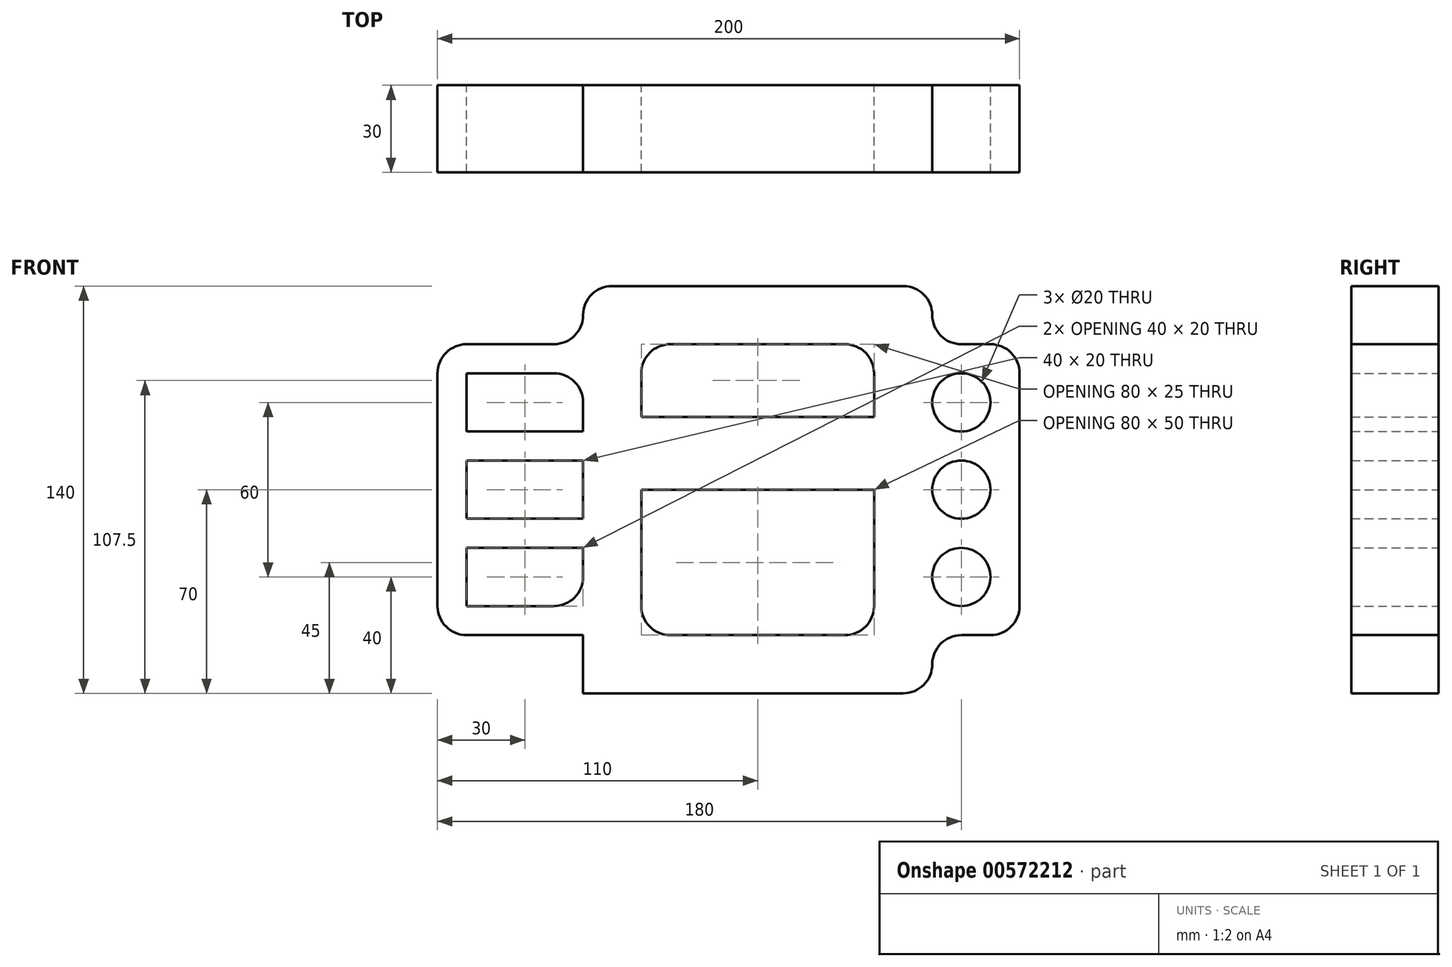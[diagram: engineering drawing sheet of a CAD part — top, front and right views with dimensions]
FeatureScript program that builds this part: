
annotation { "Feature Type Name" : "Feature", "Feature Type Description" : "" }
export const myFeature = defineFeature(function(context is Context, id is Id, definition is map)
    precondition{}
    {
        {
            var Q0;
            Q0=qCreatedBy(makeId("Front.planeOp"),FACE);
            var sketch = newSketch(context, id + "F0", { "sketchPlane" : qUnion([Q0])});
            skLineSegment(sketch, "E0", {"start": v(0, 0) * mm, "end": v(110, 0) * mm});
            skLineSegment(sketch, "E1", {"start": v(120, 10) * mm, "end": v(120, 10) * mm});
            skLineSegment(sketch, "E2", {"start": v(130, 20) * mm, "end": v(140, 20) * mm});
            skLineSegment(sketch, "E3", {"start": v(150, 30) * mm, "end": v(150, 110) * mm});
            skLineSegment(sketch, "E4", {"start": v(140, 120) * mm, "end": v(130, 120) * mm});
            skLineSegment(sketch, "E5", {"start": v(120, 130) * mm, "end": v(120, 130) * mm});
            skLineSegment(sketch, "E6", {"start": v(110, 140) * mm, "end": v(10, 140) * mm});
            skLineSegment(sketch, "E7", {"start": v(0, 130) * mm, "end": v(0, 130) * mm});
            skLineSegment(sketch, "E8", {"start": v(-10, 120) * mm, "end": v(-40, 120) * mm});
            skLineSegment(sketch, "E9", {"start": v(-50, 110) * mm, "end": v(-50, 30) * mm});
            skLineSegment(sketch, "E10", {"start": v(-40, 20) * mm, "end": v(0, 20) * mm});
            skLineSegment(sketch, "E11", {"start": v(0, 20) * mm, "end": v(0, 0) * mm});
            skLineSegment(sketch, "E12.bottom", {"start": v(20, 95) * mm, "end": v(100, 95) * mm});
            skLineSegment(sketch, "E12.top", {"start": v(30, 120) * mm, "end": v(90, 120) * mm});
            skLineSegment(sketch, "E12.left", {"start": v(20, 95) * mm, "end": v(20, 110) * mm});
            skLineSegment(sketch, "E12.right", {"start": v(100, 95) * mm, "end": v(100, 110) * mm});
            skLineSegment(sketch, "E13.bottom", {"start": v(20, 70) * mm, "end": v(100, 70) * mm});
            skLineSegment(sketch, "E13.top", {"start": v(30, 20) * mm, "end": v(90, 20) * mm});
            skLineSegment(sketch, "E13.left", {"start": v(20, 70) * mm, "end": v(20, 30) * mm});
            skLineSegment(sketch, "E13.right", {"start": v(100, 70) * mm, "end": v(100, 30) * mm});
            skLineSegment(sketch, "E14.bottom", {"start": v(-40, 110) * mm, "end": v(-10, 110) * mm});
            skLineSegment(sketch, "E14.top", {"start": v(-40, 90) * mm, "end": v(0, 90) * mm});
            skLineSegment(sketch, "E14.left", {"start": v(-40, 110) * mm, "end": v(-40, 90) * mm});
            skLineSegment(sketch, "E14.right", {"start": v(0, 100) * mm, "end": v(0, 90) * mm});
            skLineSegment(sketch, "E15.bottom", {"start": v(-40, 80) * mm, "end": v(0, 80) * mm});
            skLineSegment(sketch, "E15.top", {"start": v(-40, 60) * mm, "end": v(0, 60) * mm});
            skLineSegment(sketch, "E15.left", {"start": v(-40, 80) * mm, "end": v(-40, 60) * mm});
            skLineSegment(sketch, "E15.right", {"start": v(0, 80) * mm, "end": v(0, 60) * mm});
            skLineSegment(sketch, "E16.bottom", {"start": v(-40, 50) * mm, "end": v(0, 50) * mm});
            skLineSegment(sketch, "E16.top", {"start": v(-40, 30) * mm, "end": v(-10, 30) * mm});
            skLineSegment(sketch, "E16.left", {"start": v(-40, 50) * mm, "end": v(-40, 30) * mm});
            skLineSegment(sketch, "E16.right", {"start": v(0, 50) * mm, "end": v(0, 40) * mm});
            skCircle(sketch, "E17", {"center": v(130, 100) * mm, "radius": 10 * mm});
            skCircle(sketch, "E18", {"center": v(130, 70) * mm, "radius": 10 * mm});
            skCircle(sketch, "E19", {"center": v(130, 40) * mm, "radius": 10 * mm});
            skLineSegment(sketch, "E20", {"start": v(60, 0) * mm, "end": v(60, 20) * mm, "construction": true});
            skPoint(sketch, "E21.visualSharp", {"position": v(120, 20) * mm});
            skArc(sketch, "E21.filletArc", {"start": v(130, 20) * mm, "mid": v(122.93, 17.07) * mm, "end": v(120, 10) * mm});
            skPoint(sketch, "E22.visualSharp", {"position": v(120, 0) * mm});
            skArc(sketch, "E22.filletArc", {"start": v(110, 0) * mm, "mid": v(117.07, 2.93) * mm, "end": v(120, 10) * mm});
            skPoint(sketch, "E23.visualSharp", {"position": v(150, 20) * mm});
            skArc(sketch, "E23.filletArc", {"start": v(140, 20) * mm, "mid": v(147.07, 22.93) * mm, "end": v(150, 30) * mm});
            skPoint(sketch, "E24.visualSharp", {"position": v(150, 120) * mm});
            skArc(sketch, "E24.filletArc", {"start": v(150, 110) * mm, "mid": v(147.07, 117.07) * mm, "end": v(140, 120) * mm});
            skPoint(sketch, "E25.visualSharp", {"position": v(120, 120) * mm});
            skArc(sketch, "E25.filletArc", {"start": v(120, 130) * mm, "mid": v(122.93, 122.93) * mm, "end": v(130, 120) * mm});
            skPoint(sketch, "E26.visualSharp", {"position": v(120, 140) * mm});
            skArc(sketch, "E26.filletArc", {"start": v(120, 130) * mm, "mid": v(117.07, 137.07) * mm, "end": v(110, 140) * mm});
            skPoint(sketch, "E27.visualSharp", {"position": v(0, 140) * mm});
            skArc(sketch, "E27.filletArc", {"start": v(10, 140) * mm, "mid": v(2.93, 137.07) * mm, "end": v(0, 130) * mm});
            skPoint(sketch, "E28.visualSharp", {"position": v(0, 120) * mm});
            skArc(sketch, "E28.filletArc", {"start": v(-10, 120) * mm, "mid": v(-2.93, 122.93) * mm, "end": v(0, 130) * mm});
            skPoint(sketch, "E29.visualSharp", {"position": v(-50, 120) * mm});
            skArc(sketch, "E29.filletArc", {"start": v(-40, 120) * mm, "mid": v(-47.07, 117.07) * mm, "end": v(-50, 110) * mm});
            skPoint(sketch, "E30.visualSharp", {"position": v(-50, 20) * mm});
            skArc(sketch, "E30.filletArc", {"start": v(-50, 30) * mm, "mid": v(-47.07, 22.93) * mm, "end": v(-40, 20) * mm});
            skPoint(sketch, "E31.visualSharp", {"position": v(20, 120) * mm});
            skArc(sketch, "E31.filletArc", {"start": v(30, 120) * mm, "mid": v(22.93, 117.07) * mm, "end": v(20, 110) * mm});
            skPoint(sketch, "E32.visualSharp", {"position": v(100, 120) * mm});
            skArc(sketch, "E32.filletArc", {"start": v(100, 110) * mm, "mid": v(97.07, 117.07) * mm, "end": v(90, 120) * mm});
            skPoint(sketch, "E33.visualSharp", {"position": v(20, 20) * mm});
            skArc(sketch, "E33.filletArc", {"start": v(20, 30) * mm, "mid": v(22.93, 22.93) * mm, "end": v(30, 20) * mm});
            skPoint(sketch, "E34.visualSharp", {"position": v(100, 20) * mm});
            skArc(sketch, "E34.filletArc", {"start": v(90, 20) * mm, "mid": v(97.07, 22.93) * mm, "end": v(100, 30) * mm});
            skPoint(sketch, "E35.visualSharp", {"position": v(0, 30) * mm});
            skArc(sketch, "E35.filletArc", {"start": v(-10, 30) * mm, "mid": v(-2.93, 32.93) * mm, "end": v(0, 40) * mm});
            skPoint(sketch, "E36.visualSharp", {"position": v(0, 110) * mm});
            skArc(sketch, "E36.filletArc", {"start": v(0, 100) * mm, "mid": v(-2.93, 107.07) * mm, "end": v(-10, 110) * mm});
            skSolve(sketch);
        }
        {
            var Q0;
            Q0 = qSketchRegion(id + "F0", true);
            extrude(context, id + "F1", {"entities" : qUnion([Q0]), "depth" : 30 * mm, "offsetDistance" : 25 * mm});
        }
    });
